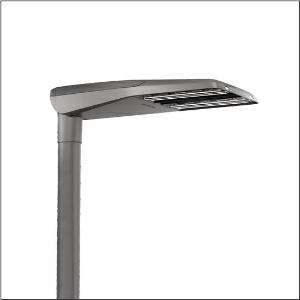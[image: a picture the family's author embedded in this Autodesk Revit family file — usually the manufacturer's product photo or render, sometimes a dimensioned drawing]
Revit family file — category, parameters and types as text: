
# Revit family: streetlight_sl_11_iq_midi___st1_0ab_5xc3n41f08le_a448
name_source: partatom
category: Lighting Fixtures
units: mm (PartAtom-declared; Revit-internal decimal feet)

## family parameters
Cut with Voids When Loaded = No
Host = Face
Light Source = No
Part Type = Normal
Room Calculation Point = No
Round Connector Dimension = Use Diameter
Shared = No

## types (1)
- --- (1 x LED, 8080 lm, 60.4 W, 4000K)
    Apparent Load = 60 VA
    CIE Flux Codes = 29 63 95 100 100
    Color Rendering = 70
    Color Temperature = 4000K
    Default Elevation = 1800 mm
    Description = Streetlight SL 11 iQ midi, mast luminaire, primary light control with 3 zone facetted reflector, of plastic, silver coated, highly specular, primary optical cover: cover, of PMMA, transparent, light distribution: ST1.0aB, light emission: direct distribution, primary light characteristic: asymmetric, installation type: post-top, side-entry, LED, High Power LED, rated luminous flux: 8.080lm, luminous efficacy: 134lm/W, light colour: 740, colour temperature: 4000K, control: optimised constant luminous flux control (CLO 2.0), Street-Remote, Desk-Remote (wireless, voltage-free reading and setting of iQ features in the workshop via application-optimized NFC function/RFID function), Light-Fading, Smart-Wire, Night-Set, Lumen-Switch, Temp-Guard, Auto-Match, with cable H07RN-F 5x 1.5mm², mains connection: 230..240V, AC, 50/60Hz, connection cable pre-assembled, cable length: 8,5m, start of lifetime: 60W, end of service life: 63W, reduction: 30W, luminaire housing, of diecast aluminium, powder-coated, Siteco® metallic grey (DB 702S), please order mast flange separately, inclination adjustable without tools: 0°, 5°, 10°, 15° (post-top) | 0°, -5°, -10°, -15° (side-entry), sealing non-destructively replaceable, multi-level sealing system, length: 780mm, width: 376mm, height: 118mm, mast flange for spigot size: 42mm (side-entry): 5XC10008XM4, 60/48mm (side-entry/post-top): 5XC10108XM2, 76/60mm (side-entry/post-top): 5XC10108XM1, equipment: standard, protection rating (complete): IP66, insulation class (complete): insulation class II (safety insulation), certification: CE, ENEC, VDE, impact resistance: IK09, permissible operating ambient temperature for outdoor applications: -25..+50°C, standard-compliant lighting for roads and squares, Environmental Product Declaration (EPD) tested and certified by an independent institute, packaging unit: 1 piece

Light Distribution: ST1.0aB
    Height = 118 mm
    Lamp = 1 x LED
    Lamp Light Flux = 8080 lm
    Lamp Power = 60.4 W
    Lamp count = 1
    Length = 780 mm
    Luminous efficacy = 134 lm/W
    Manufacturer = Siteco
    ModVariant = No
    Model = 5XC3N41F08LE
    Number of Poles = 1
    OnlyDefault = Yes
    Power Factor = 1
    Product Name = Streetlight SL 11 iQ midi | ST1.0aB
    Product group = mast luminaire | pylon top
    ProductGroupID = 6100
    Protection Class = Protection class II
    Protection Degree = IP 66
    RLX_Detail_Level = 1
    RLX_Emergency_Light_Flux = 0 lm
    RLX_Emergency_Type = 0
    RLX_Emergency_Type_DB = No
    RlxData = <blob elided: 70077 chars, md5=13479d30>
    Socket = socket
    Standby Power = 0 W
    System Light Flux = 8080 lm
    System Power = 60 W
    Type Comments = factory setting: luminous flux: 100 % | dim-lin: 254 | 520 mA
    Type Image = l_1005960.jpg
    URL = http://relux.com
    VarID = @adj_020259
    Voltage = 0 V
    Weight = 0.00 kg
    Width = 376 mm

## geometry (parser evidence)
native form markers: Blend x4, Sweep x9
no freeform markers — native parametric forms only
